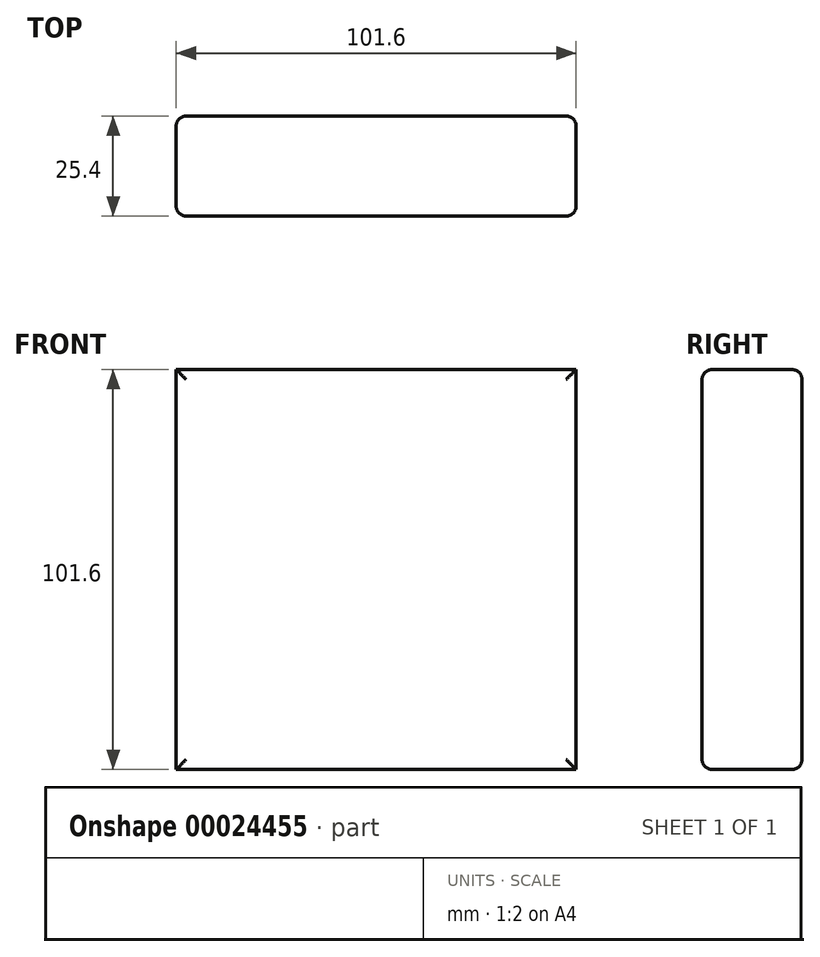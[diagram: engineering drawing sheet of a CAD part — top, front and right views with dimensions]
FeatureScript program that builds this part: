
annotation { "Feature Type Name" : "Feature", "Feature Type Description" : "" }
export const myFeature = defineFeature(function(context is Context, id is Id, definition is map)
    precondition{}
    {
        {
            var Q0;
            Q0=qCreatedBy(makeId("Front.planeOp"),FACE);
            var sketch = newSketch(context, id + "F0", { "sketchPlane" : qUnion([Q0])});
            skLineSegment(sketch, "E0.bottom", {"start": v(-50.5, 53.15) * mm, "end": v(51.1, 53.15) * mm});
            skLineSegment(sketch, "E0.top", {"start": v(-50.5, -48.45) * mm, "end": v(51.1, -48.45) * mm});
            skLineSegment(sketch, "E0.left", {"start": v(-50.5, 53.15) * mm, "end": v(-50.5, -48.45) * mm});
            skLineSegment(sketch, "E0.right", {"start": v(51.1, 53.15) * mm, "end": v(51.1, -48.45) * mm});
            skSolve(sketch);
        }
        {
            var Q0;
            Q0=makeQuery(id+"F0.imprint","IMPRINT",FACE,{"disambiguationData":[TD([[makeQuery(id+"F0.imprint","IMPRINT",EDGE,{"derivedFrom":sQuery(id+"F0.wireOp",EDGE,"E0.bottom")}),-1.0]])]});
            extrude(context, id + "F1", {"entities" : qUnion([Q0]), "depth" : 25.4 * mm});
        }
        {
            var Q0;
            Q0=makeQuery(id+"F1.opExtrude","CAP_FACE",FACE,{"disambiguationData":[OSD([sQuery(id+"F0.wireOp",EDGE,"E0.bottom"),sQuery(id+"F0.wireOp",EDGE,"E0.top"),sQuery(id+"F0.wireOp",EDGE,"E0.left"),sQuery(id+"F0.wireOp",EDGE,"E0.right")])],"isStart":false});
            var Q1;
            Q1=makeQuery(id+"F1.opExtrude","CAP_FACE",FACE,{"disambiguationData":[OSD([sQuery(id+"F0.wireOp",EDGE,"E0.bottom"),sQuery(id+"F0.wireOp",EDGE,"E0.top"),sQuery(id+"F0.wireOp",EDGE,"E0.left"),sQuery(id+"F0.wireOp",EDGE,"E0.right")])],"isStart":true});
            fillet(context, id + "F2", {"entities" : qUnion([Q0, Q1]), "radius" : 2.54 * mm, "tangentPropagation" : true, "allowEdgeOverflow" : false});
        }
    });
